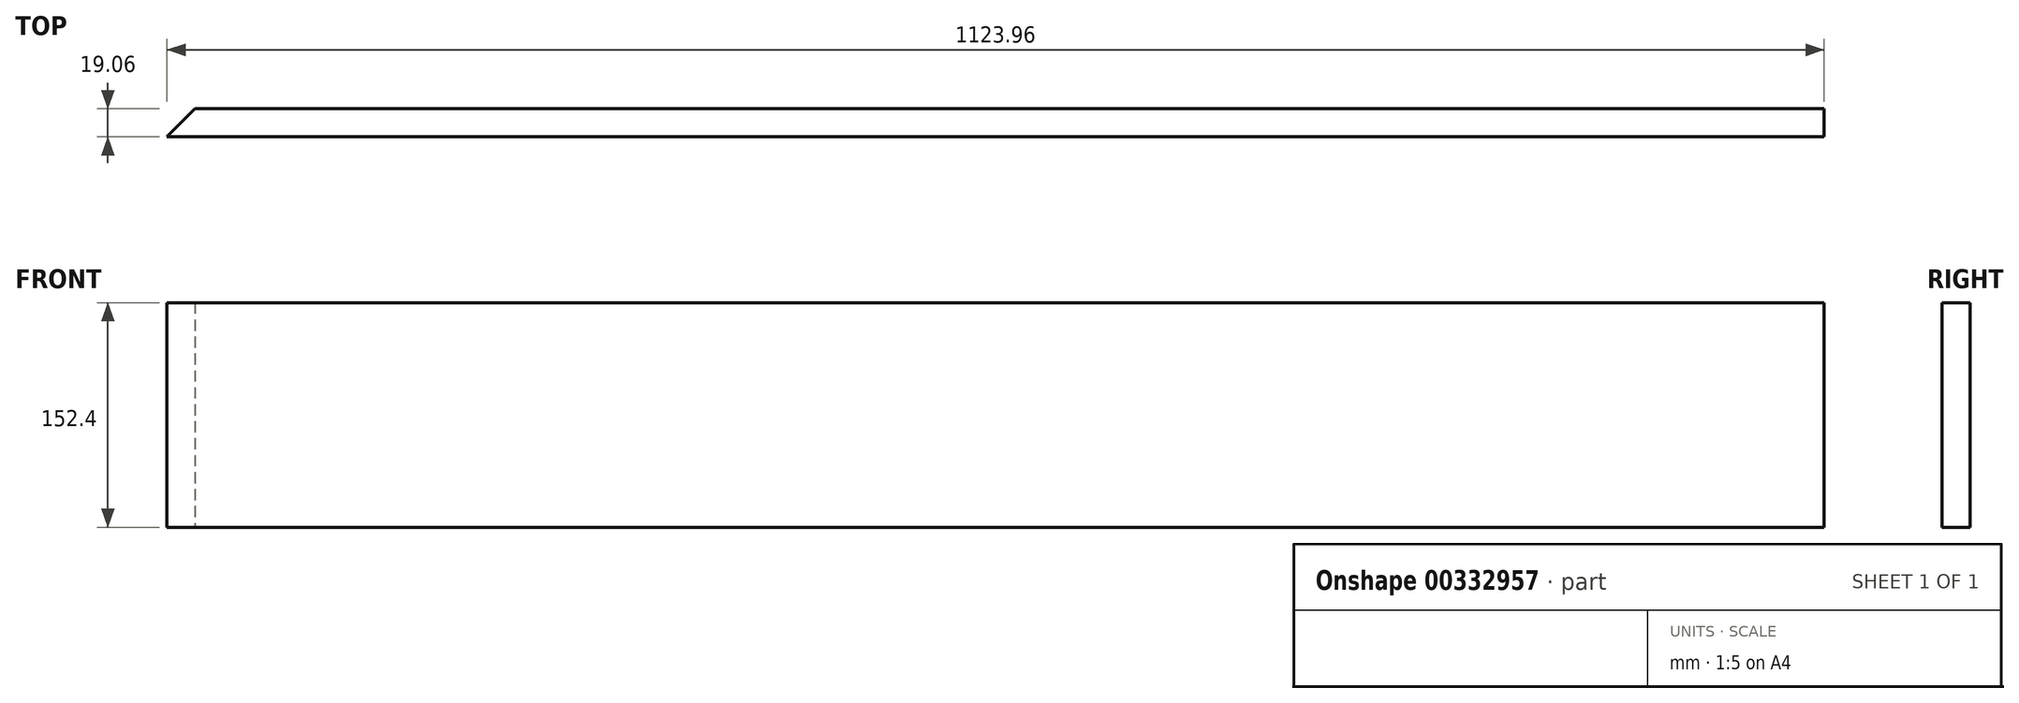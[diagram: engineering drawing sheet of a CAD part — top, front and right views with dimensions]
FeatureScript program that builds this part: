
annotation { "Feature Type Name" : "Feature", "Feature Type Description" : "" }
export const myFeature = defineFeature(function(context is Context, id is Id, definition is map)
    precondition{}
    {
        {
            var Q0;
            Q0=qCreatedBy(makeId("Top.planeOp"),FACE);
            var sketch = newSketch(context, id + "F0", { "sketchPlane" : qUnion([Q0])});
            skLineSegment(sketch, "E0.bottom", {"start": v(-561.98, -9.53) * mm, "end": v(561.97, -9.53) * mm});
            skLineSegment(sketch, "E0.top", {"start": v(-542.93, 9.52) * mm, "end": v(561.98, 9.52) * mm});
            skLineSegment(sketch, "E0.right", {"start": v(561.97, -9.53) * mm, "end": v(561.98, 9.52) * mm});
            skPoint(sketch, "E0.middle", {"position": v(0, 0) * mm});
            skLineSegment(sketch, "E1", {"start": v(-561.98, -9.53) * mm, "end": v(-542.93, 9.53) * mm});
            skPoint(sketch, "E0.left.end.orphan", {"position": v(-561.97, 9.52) * mm});
            skSolve(sketch);
        }
        {
            var Q0;
            Q0 = qSketchRegion(id + "F0", true);
            extrude(context, id + "F1", {"entities" : qUnion([Q0]), "depth" : 152.4 * mm});
        }
    });
